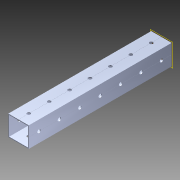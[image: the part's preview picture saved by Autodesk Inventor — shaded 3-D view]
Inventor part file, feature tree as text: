
AUTODESK INVENTOR PART (.ipt)
format: ipt  version: 2014 (Build 180170000, 170)  size: 1,210,368 bytes
history: native  units: in
note: dims shown in document units (in); Inventor stores cm internally (conversion verified against a paired STEP export)
features: extrude x3, sketch x3, pattern_circular x1, other x1, plane x1, imported_body x1
ambient origin geometry x8: Origin, YZ Plane, XZ Plane, XY Plane, X Axis, Y Axis, Z Axis, Center Point
bodies: Body1 (feature_tree)
feature tree (10):
  pattern_circular  "CirPattern2"
  other  "217-3426-STEP1"
  plane  "Work Plane1"
  extrude  "Extrusion1"  Depth=3937.0079in TaperAngle=0.0deg
  extrude  "Extrusion2"  Depth=1.0in TaperAngle=0.0deg
  extrude  "Extrusion3"  [1 undecoded]
  imported_body  "Base1"
  sketch  "Sketch1"  dims[d0=-21.0in d1=3937.0079in d2=0.0in]
  sketch  "Sketch3"  dims[d3=1.0in d4=0.0in d5=13.0in d6=0.0in]
  sketch  "Sketch4"
note: 1 required parameter value undecoded (feature->parameter linkage not recoverable at this tier; creation-order binding heuristic only, values carry confidence <= 0.55)
